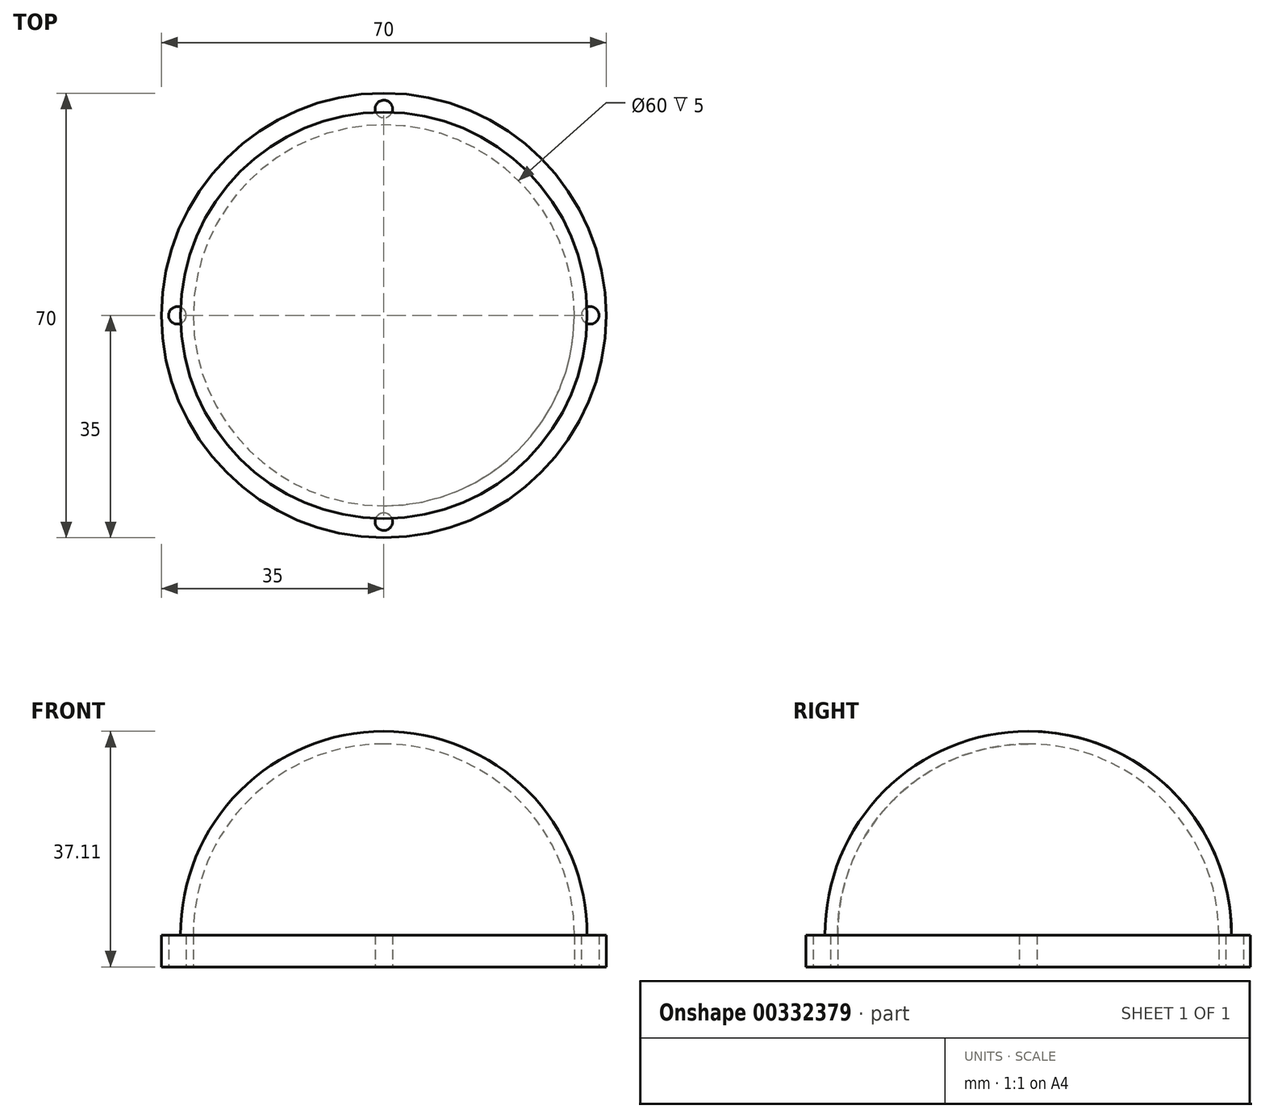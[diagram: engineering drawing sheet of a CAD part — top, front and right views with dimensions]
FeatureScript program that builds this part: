
annotation { "Feature Type Name" : "Feature", "Feature Type Description" : "" }
export const myFeature = defineFeature(function(context is Context, id is Id, definition is map)
    precondition{}
    {
        {
            var Q0;
            Q0=qCreatedBy(makeId("Top.planeOp"),FACE);
            var sketch = newSketch(context, id + "F0", { "sketchPlane" : qUnion([Q0])});
            skCircle(sketch, "E0", {"center": v(0, 0) * mm, "radius": 30 * mm});
            skCircle(sketch, "E1", {"center": v(0, 0) * mm, "radius": 35 * mm});
            skSolve(sketch);
        }
        {
            var Q0;
            Q0=makeQuery(id+"F0.imprint","IMPRINT",FACE,{"disambiguationData":[TD([[makeQuery(id+"F0.imprint","IMPRINT",EDGE,{"derivedFrom":sQuery(id+"F0.wireOp",EDGE,"E0")}),-1.0]])]});
            extrude(context, id + "F1", {"entities" : qUnion([Q0]), "depth" : 5 * mm});
        }
        {
            var Q0;
            Q0=qCreatedBy(makeId("Top.planeOp"),FACE);
            var sketch = newSketch(context, id + "F2", { "sketchPlane" : qUnion([Q0])});
            skCircle(sketch, "E2", {"center": v(0, 0) * mm, "radius": 32.5 * mm});
            skCircle(sketch, "E3", {"center": v(0, 32.5) * mm, "radius": 1.38 * mm});
            skCircle(sketch, "E4.1.0", {"center": v(-32.5, 0) * mm, "radius": 1.38 * mm});
            skCircle(sketch, "E4.2.0", {"center": v(0, -32.5) * mm, "radius": 1.38 * mm});
            skCircle(sketch, "E4.3.0", {"center": v(32.5, 0) * mm, "radius": 1.38 * mm});
            skSolve(sketch);
        }
        {
            var Q0;
            {var subQ0=sQuery(id+"F2.wireOp",EDGE,"E3");var subQ1=sQuery(id+"F2.wireOp",EDGE,"E2");var subQ2=makeQuery(id+"F2.imprint","INTERSECT",VERTEX,{"disambiguationData":[OD(0.0)],"derivedFrom":[subQ1,subQ0]});Q0=makeQuery(id+"F2.imprint","IMPRINT",FACE,{"disambiguationData":[TD([[makeQuery(id+"F2.imprint","IMPRINT",EDGE,{"disambiguationData":[TD([[subQ2,-1.0]])],"derivedFrom":subQ1}),-1.0]])]});}
            var Q1;
            {var subQ0=sQuery(id+"F2.wireOp",EDGE,"E3");var subQ1=sQuery(id+"F2.wireOp",EDGE,"E2");var subQ2=makeQuery(id+"F2.imprint","INTERSECT",VERTEX,{"disambiguationData":[OD(0.0)],"derivedFrom":[subQ1,subQ0]});Q1=makeQuery(id+"F2.imprint","IMPRINT",FACE,{"disambiguationData":[TD([[makeQuery(id+"F2.imprint","IMPRINT",EDGE,{"disambiguationData":[TD([[subQ2,-1.0]])],"derivedFrom":subQ1}),1.0]])]});}
            var Q2;
            {var subQ0=sQuery(id+"F2.wireOp",EDGE,"E4.3.0");var subQ1=sQuery(id+"F2.wireOp",EDGE,"E2");var subQ2=makeQuery(id+"F2.imprint","INTERSECT",VERTEX,{"disambiguationData":[OD(0.0)],"derivedFrom":[subQ1,subQ0]});Q2=makeQuery(id+"F2.imprint","IMPRINT",FACE,{"disambiguationData":[TD([[makeQuery(id+"F2.imprint","IMPRINT",EDGE,{"disambiguationData":[TD([[subQ2,1.0]])],"derivedFrom":subQ1}),-1.0]])]});}
            var Q3;
            {var subQ0=sQuery(id+"F2.wireOp",EDGE,"E4.3.0");var subQ1=sQuery(id+"F2.wireOp",EDGE,"E2");var subQ2=makeQuery(id+"F2.imprint","INTERSECT",VERTEX,{"disambiguationData":[OD(0.0)],"derivedFrom":[subQ1,subQ0]});Q3=makeQuery(id+"F2.imprint","IMPRINT",FACE,{"disambiguationData":[TD([[makeQuery(id+"F2.imprint","IMPRINT",EDGE,{"disambiguationData":[TD([[subQ2,1.0]])],"derivedFrom":subQ1}),1.0]])]});}
            var Q4;
            {var subQ0=sQuery(id+"F2.wireOp",EDGE,"E4.1.0");var subQ1=sQuery(id+"F2.wireOp",EDGE,"E2");var subQ2=makeQuery(id+"F2.imprint","INTERSECT",VERTEX,{"disambiguationData":[OD(0.0)],"derivedFrom":[subQ1,subQ0]});Q4=makeQuery(id+"F2.imprint","IMPRINT",FACE,{"disambiguationData":[TD([[makeQuery(id+"F2.imprint","IMPRINT",EDGE,{"disambiguationData":[TD([[subQ2,-1.0]])],"derivedFrom":subQ1}),-1.0]])]});}
            var Q5;
            {var subQ0=sQuery(id+"F2.wireOp",EDGE,"E4.1.0");var subQ1=sQuery(id+"F2.wireOp",EDGE,"E2");var subQ2=makeQuery(id+"F2.imprint","INTERSECT",VERTEX,{"disambiguationData":[OD(0.0)],"derivedFrom":[subQ1,subQ0]});Q5=makeQuery(id+"F2.imprint","IMPRINT",FACE,{"disambiguationData":[TD([[makeQuery(id+"F2.imprint","IMPRINT",EDGE,{"disambiguationData":[TD([[subQ2,-1.0]])],"derivedFrom":subQ1}),1.0]])]});}
            var Q6;
            {var subQ0=sQuery(id+"F2.wireOp",EDGE,"E4.2.0");var subQ1=sQuery(id+"F2.wireOp",EDGE,"E2");var subQ2=makeQuery(id+"F2.imprint","INTERSECT",VERTEX,{"disambiguationData":[OD(0.0)],"derivedFrom":[subQ1,subQ0]});Q6=makeQuery(id+"F2.imprint","IMPRINT",FACE,{"disambiguationData":[TD([[makeQuery(id+"F2.imprint","IMPRINT",EDGE,{"disambiguationData":[TD([[subQ2,-1.0]])],"derivedFrom":subQ1}),-1.0]])]});}
            var Q7;
            {var subQ0=sQuery(id+"F2.wireOp",EDGE,"E4.2.0");var subQ1=sQuery(id+"F2.wireOp",EDGE,"E2");var subQ2=makeQuery(id+"F2.imprint","INTERSECT",VERTEX,{"disambiguationData":[OD(0.0)],"derivedFrom":[subQ1,subQ0]});Q7=makeQuery(id+"F2.imprint","IMPRINT",FACE,{"disambiguationData":[TD([[makeQuery(id+"F2.imprint","IMPRINT",EDGE,{"disambiguationData":[TD([[subQ2,-1.0]])],"derivedFrom":subQ1}),1.0]])]});}
            var Q8;
            Q8=sQuery(id+"F2.wireOp",EDGE,"E3");
            extrude(context, id + "F3", {"entities" : qUnion([Q0, Q1, Q2, Q3, Q4, Q5, Q6, Q7]), "operationType" : NewBodyOperationType.REMOVE, "surfaceEntities" : qUnion([Q8]), "depth" : 25 * mm});
        }
        {
            var Q0;
            Q0=qCreatedBy(makeId("Right.planeOp"),FACE);
            var sketch = newSketch(context, id + "F4", { "sketchPlane" : qUnion([Q0])});
            skArc(sketch, "E5", {"start": v(0, 35.11) * mm, "mid": v(-21.24, 26.3) * mm, "end": v(-30, 5.02) * mm});
            skArc(sketch, "E6", {"start": v(0, 37.11) * mm, "mid": v(-22.66, 27.7) * mm, "end": v(-32, 5.01) * mm});
            skLineSegment(sketch, "E7", {"start": v(0, 37.11) * mm, "end": v(0, 35.11) * mm});
            skPoint(sketch, "E8.orphan", {"position": v(-32, 5.11) * mm});
            skLineSegment(sketch, "E9", {"start": v(-30, 5.02) * mm, "end": v(-32, 5.01) * mm});
            skSolve(sketch);
        }
        {
            var Q0;
            Q0=makeQuery(id+"F4.imprint","IMPRINT",FACE,{"disambiguationData":[TD([[makeQuery(id+"F4.imprint","IMPRINT",EDGE,{"derivedFrom":sQuery(id+"F4.wireOp",EDGE,"E5")}),-1.0]])]});
            var Q1;
            Q1=sQuery(id+"F4.wireOp",EDGE,"E7");
            revolve(context, id + "F5", {"entities" : qUnion([Q0]), "axis" : qUnion([Q1]), "revolveType" : RevolveType.FULL});
        }
    });
